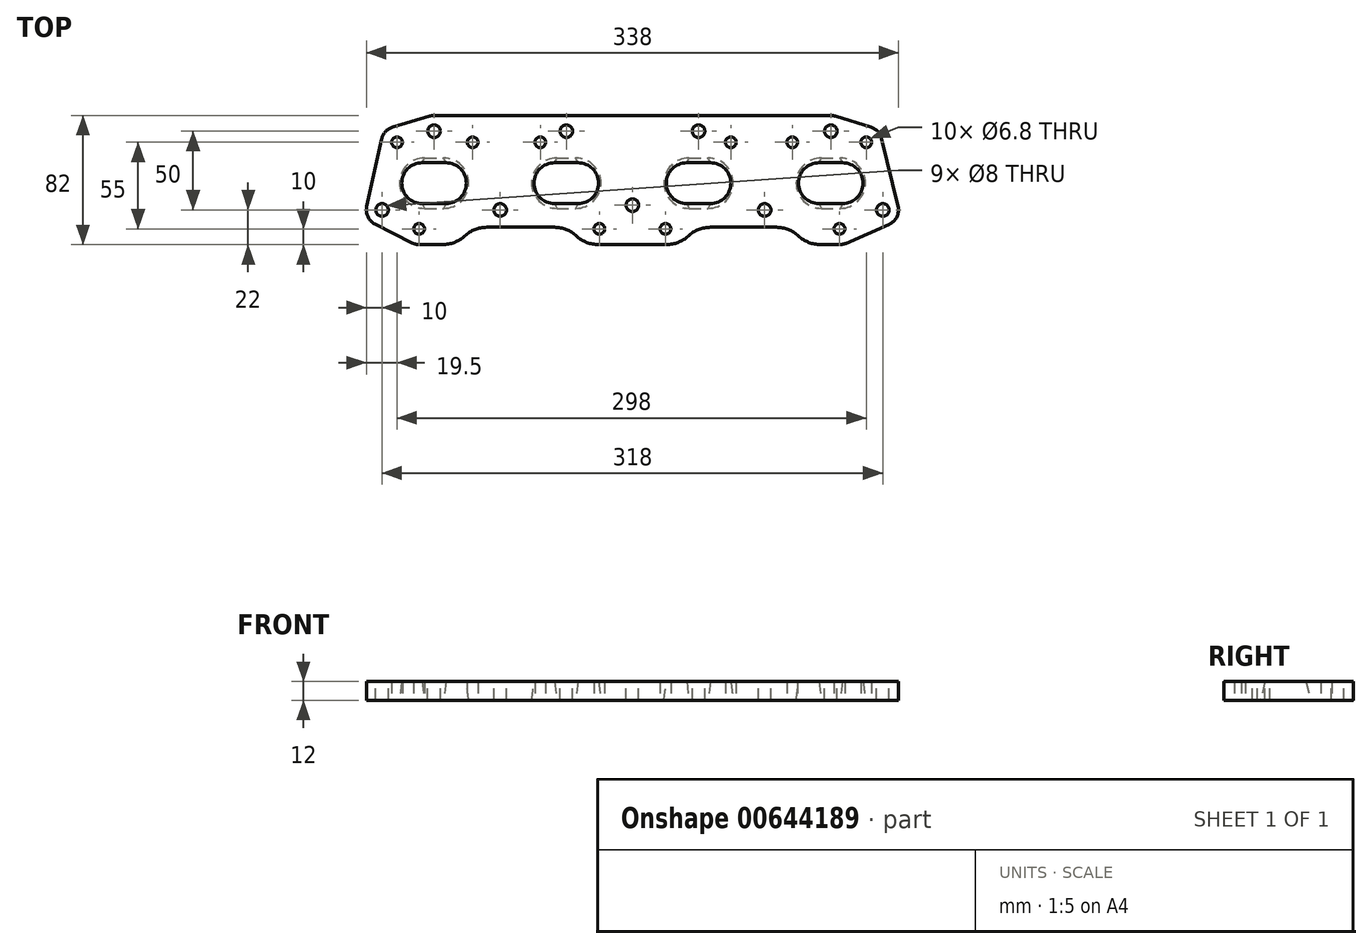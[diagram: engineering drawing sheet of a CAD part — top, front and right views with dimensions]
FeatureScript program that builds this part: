
annotation { "Feature Type Name" : "Feature", "Feature Type Description" : "" }
export const myFeature = defineFeature(function(context is Context, id is Id, definition is map)
    precondition{}
    {
        {
            var Q0;
            Q0=qCreatedBy(makeId("Top.planeOp"),FACE);
            var sketch = newSketch(context, id + "F0", { "sketchPlane" : qUnion([Q0])});
            skCircle(sketch, "E0", {"center": v(-17.5, 26) * mm, "radius": 5 * mm, "construction": true});
            skCircle(sketch, "E1", {"center": v(-3.5, -29) * mm, "radius": 5 * mm, "construction": true});
            skCircle(sketch, "E2", {"center": v(30.5, 26) * mm, "radius": 5 * mm, "construction": true});
            skCircle(sketch, "E3", {"center": v(73.5, 26) * mm, "radius": 5 * mm, "construction": true});
            skCircle(sketch, "E4", {"center": v(194.5, 26) * mm, "radius": 5 * mm, "construction": true});
            skCircle(sketch, "E5", {"center": v(233.5, 26) * mm, "radius": 5 * mm, "construction": true});
            skCircle(sketch, "E6", {"center": v(280.5, 26) * mm, "radius": 4 * mm, "construction": true});
            skCircle(sketch, "E7", {"center": v(111, -29) * mm, "radius": 4 * mm, "construction": true});
            skCircle(sketch, "E8", {"center": v(153, -29) * mm, "radius": 5 * mm, "construction": true});
            skCircle(sketch, "E9", {"center": v(263.5, -29) * mm, "radius": 5 * mm, "construction": true});
            skLineSegment(sketch, "E10", {"start": v(0, 0) * mm, "end": v(46.38, 0) * mm, "construction": true});
            skCircle(sketch, "E11", {"center": v(-17.5, 26) * mm, "radius": 10 * mm, "construction": true});
            skCircle(sketch, "E12", {"center": v(-3.5, -29) * mm, "radius": 10 * mm, "construction": true});
            skCircle(sketch, "E13", {"center": v(263.5, -29) * mm, "radius": 10 * mm, "construction": true});
            skCircle(sketch, "E14", {"center": v(280.5, 26) * mm, "radius": 10 * mm, "construction": true});
            skCircle(sketch, "E15", {"center": v(6, 33) * mm, "radius": 4 * mm, "construction": true});
            skCircle(sketch, "E16", {"center": v(-27, -17) * mm, "radius": 4 * mm, "construction": true});
            skCircle(sketch, "E17", {"center": v(90, 33) * mm, "radius": 4 * mm, "construction": true});
            skCircle(sketch, "E18", {"center": v(174, 33) * mm, "radius": 4 * mm, "construction": true});
            skCircle(sketch, "E19", {"center": v(258, 33) * mm, "radius": 4 * mm, "construction": true});
            skCircle(sketch, "E20", {"center": v(48, -17) * mm, "radius": 4 * mm, "construction": true});
            skCircle(sketch, "E21", {"center": v(132, -14) * mm, "radius": 4 * mm, "construction": true});
            skCircle(sketch, "E22", {"center": v(216, -17) * mm, "radius": 4 * mm, "construction": true});
            skCircle(sketch, "E23", {"center": v(291, -17) * mm, "radius": 4 * mm, "construction": true});
            skCircle(sketch, "E24", {"center": v(6, 33) * mm, "radius": 10 * mm, "construction": true});
            skCircle(sketch, "E25", {"center": v(258, 33) * mm, "radius": 10 * mm, "construction": true});
            skCircle(sketch, "E26", {"center": v(-27, -17) * mm, "radius": 10 * mm, "construction": true});
            skCircle(sketch, "E27", {"center": v(291, -17) * mm, "radius": 10 * mm, "construction": true});
            skLineSegment(sketch, "E28", {"start": v(3.15, 42.58) * mm, "end": v(-20.35, 35.58) * mm});
            skLineSegment(sketch, "E29", {"start": v(-27.26, 28.16) * mm, "end": v(-36.76, -14.84) * mm});
            skLineSegment(sketch, "E30", {"start": v(-31.55, -25.9) * mm, "end": v(-8.05, -37.9) * mm});
            skLineSegment(sketch, "E31", {"start": v(267.5, -38.17) * mm, "end": v(295, -26.17) * mm});
            skLineSegment(sketch, "E32", {"start": v(300.71, -14.63) * mm, "end": v(290.21, 28.37) * mm});
            skLineSegment(sketch, "E33", {"start": v(283.47, 35.55) * mm, "end": v(260.97, 42.55) * mm});
            skArc(sketch, "E34", {"start": v(6, 43) * mm, "mid": v(4.56, 42.9) * mm, "end": v(3.15, 42.58) * mm});
            skArc(sketch, "E35", {"start": v(-20.35, 35.58) * mm, "mid": v(-24.82, 32.81) * mm, "end": v(-27.26, 28.16) * mm});
            skArc(sketch, "E36", {"start": v(-36.76, -14.84) * mm, "mid": v(-36.04, -21.26) * mm, "end": v(-31.55, -25.9) * mm});
            skArc(sketch, "E37", {"start": v(-8.05, -37.9) * mm, "mid": v(-5.84, -38.72) * mm, "end": v(-3.5, -39) * mm});
            skArc(sketch, "E38", {"start": v(263.45, -39) * mm, "mid": v(265.52, -38.8) * mm, "end": v(267.5, -38.17) * mm});
            skArc(sketch, "E39", {"start": v(295, -26.17) * mm, "mid": v(299.96, -21.44) * mm, "end": v(300.71, -14.63) * mm});
            skArc(sketch, "E40", {"start": v(290.21, 28.37) * mm, "mid": v(287.79, 32.85) * mm, "end": v(283.47, 35.55) * mm});
            skArc(sketch, "E41", {"start": v(260.97, 42.55) * mm, "mid": v(259.5, 42.89) * mm, "end": v(258, 43) * mm});
            skLineSegment(sketch, "E42", {"start": v(-67.09, -28) * mm, "end": v(306.12, -28) * mm, "construction": true});
            skLineSegment(sketch, "E43", {"start": v(-3.5, -39) * mm, "end": v(11.5, -39) * mm});
            skLineSegment(sketch, "E44", {"start": v(263.45, -39) * mm, "end": v(251.45, -39) * mm});
            skLineSegment(sketch, "E45", {"start": v(110.44, -39) * mm, "end": v(153.53, -39) * mm});
            skLineSegment(sketch, "E46", {"start": v(-51.35, -33.5) * mm, "end": v(297.43, -33.5) * mm, "construction": true});
            skArc(sketch, "E47", {"start": v(11.5, -39) * mm, "mid": v(19.02, -37.58) * mm, "end": v(25.5, -33.5) * mm});
            skArc(sketch, "E48", {"start": v(39.5, -28) * mm, "mid": v(31.98, -29.42) * mm, "end": v(25.5, -33.5) * mm});
            skArc(sketch, "E49", {"start": v(96.44, -33.5) * mm, "mid": v(102.92, -37.58) * mm, "end": v(110.44, -39) * mm});
            skArc(sketch, "E50", {"start": v(96.44, -33.5) * mm, "mid": v(89.96, -29.42) * mm, "end": v(82.44, -28) * mm});
            skArc(sketch, "E51", {"start": v(153.53, -39) * mm, "mid": v(161.05, -37.58) * mm, "end": v(167.53, -33.5) * mm});
            skArc(sketch, "E52", {"start": v(181.53, -28) * mm, "mid": v(174, -29.42) * mm, "end": v(167.53, -33.5) * mm});
            skArc(sketch, "E53", {"start": v(237.45, -33.5) * mm, "mid": v(243.92, -37.58) * mm, "end": v(251.45, -39) * mm});
            skArc(sketch, "E54", {"start": v(237.45, -33.5) * mm, "mid": v(230.97, -29.42) * mm, "end": v(223.45, -28) * mm});
            skLineSegment(sketch, "E55", {"start": v(39.5, -28) * mm, "end": v(82.44, -28) * mm});
            skLineSegment(sketch, "E56", {"start": v(181.53, -28) * mm, "end": v(223.45, -28) * mm});
            skLineSegment(sketch, "E57", {"start": v(258, 43) * mm, "end": v(6, 43) * mm});
            skSolve(sketch);
        }
        {
            var Q0;
            Q0=qCreatedBy(makeId("Top.planeOp"),FACE);
            var sketch = newSketch(context, id + "F1", { "sketchPlane" : qUnion([Q0])});
            skArc(sketch, "E58", {"start": v(0, 16) * mm, "mid": v(-16, 0) * mm, "end": v(0, -16) * mm});
            skLineSegment(sketch, "E59", {"start": v(0, 16) * mm, "end": v(12, 16) * mm});
            skArc(sketch, "E60", {"start": v(12, -16) * mm, "mid": v(28, 0) * mm, "end": v(12, 16) * mm});
            skLineSegment(sketch, "E61", {"start": v(0, -16) * mm, "end": v(12, -16) * mm});
            skArc(sketch, "E62.1.0.0", {"start": v(96, -16) * mm, "mid": v(112, 0) * mm, "end": v(96, 16) * mm});
            skArc(sketch, "E62.1.0.1", {"start": v(84, 16) * mm, "mid": v(68, 0) * mm, "end": v(84, -16) * mm});
            skLineSegment(sketch, "E62.1.0.2", {"start": v(84, -16) * mm, "end": v(96, -16) * mm});
            skLineSegment(sketch, "E62.1.0.3", {"start": v(84, 16) * mm, "end": v(96, 16) * mm});
            skArc(sketch, "E62.2.0.0", {"start": v(180, -16) * mm, "mid": v(196, 0) * mm, "end": v(180, 16) * mm});
            skArc(sketch, "E62.2.0.1", {"start": v(168, 16) * mm, "mid": v(152, 0) * mm, "end": v(168, -16) * mm});
            skLineSegment(sketch, "E62.2.0.2", {"start": v(168, -16) * mm, "end": v(180, -16) * mm});
            skLineSegment(sketch, "E62.2.0.3", {"start": v(168, 16) * mm, "end": v(180, 16) * mm});
            skArc(sketch, "E62.3.0.0", {"start": v(264, -16) * mm, "mid": v(280, 0) * mm, "end": v(264, 16) * mm});
            skArc(sketch, "E62.3.0.1", {"start": v(252, 16) * mm, "mid": v(236, 0) * mm, "end": v(252, -16) * mm});
            skLineSegment(sketch, "E62.3.0.2", {"start": v(252, -16) * mm, "end": v(264, -16) * mm});
            skLineSegment(sketch, "E62.3.0.3", {"start": v(252, 16) * mm, "end": v(264, 16) * mm});
            skLineSegment(sketch, "E62.direction1", {"start": v(0, -16) * mm, "end": v(84, -16) * mm, "construction": true});
            skCircle(sketch, "E63", {"center": v(6, 33) * mm, "radius": 4 * mm});
            skCircle(sketch, "E64", {"center": v(-27, -17) * mm, "radius": 4 * mm});
            skCircle(sketch, "E65", {"center": v(90, 33) * mm, "radius": 4 * mm});
            skCircle(sketch, "E66", {"center": v(174, 33) * mm, "radius": 4 * mm});
            skCircle(sketch, "E67", {"center": v(258, 33) * mm, "radius": 4 * mm});
            skCircle(sketch, "E68", {"center": v(48, -17) * mm, "radius": 4 * mm});
            skCircle(sketch, "E69", {"center": v(132, -14) * mm, "radius": 4 * mm});
            skCircle(sketch, "E70", {"center": v(216, -17) * mm, "radius": 4 * mm});
            skCircle(sketch, "E71", {"center": v(291, -17) * mm, "radius": 4 * mm});
            skSolve(sketch);
        }
        {
            var Q0;
            Q0=qCreatedBy(makeId("Top.planeOp"),FACE);
            cPlane(context, id + "F2", {"entities" : qUnion([Q0]), "cplaneType" : CPlaneType.OFFSET, "offset" : 12 * mm, "width" : 150 * mm, "height" : 150 * mm});
        }
        {
            var Q0;
            Q0=qCreatedBy(id+"F2.planeOp",FACE);
            var sketch = newSketch(context, id + "F3", { "sketchPlane" : qUnion([Q0]), "disableImprinting" : false});
            skCircle(sketch, "E72", {"center": v(-17.5, 26) * mm, "radius": 5 * mm});
            skCircle(sketch, "E73", {"center": v(-3.5, -29) * mm, "radius": 5 * mm});
            skCircle(sketch, "E74", {"center": v(30.5, 26) * mm, "radius": 5 * mm});
            skCircle(sketch, "E75", {"center": v(73.5, 26) * mm, "radius": 5 * mm});
            skCircle(sketch, "E76", {"center": v(194.5, 26) * mm, "radius": 5 * mm});
            skCircle(sketch, "E77", {"center": v(233.5, 26) * mm, "radius": 5 * mm});
            skCircle(sketch, "E78", {"center": v(280.5, 26) * mm, "radius": 4 * mm});
            skCircle(sketch, "E79", {"center": v(111, -29) * mm, "radius": 4 * mm});
            skCircle(sketch, "E80", {"center": v(153, -29) * mm, "radius": 5 * mm});
            skCircle(sketch, "E81", {"center": v(263.5, -29) * mm, "radius": 5 * mm});
            skArc(sketch, "E82", {"start": v(-1.5, 13) * mm, "mid": v(-14.5, 0) * mm, "end": v(-1.5, -13) * mm});
            skArc(sketch, "E83", {"start": v(13.5, -13) * mm, "mid": v(26.5, 0) * mm, "end": v(13.5, 13) * mm});
            skArc(sketch, "E84", {"start": v(97.5, -13) * mm, "mid": v(110.5, 0) * mm, "end": v(97.5, 13) * mm});
            skArc(sketch, "E85", {"start": v(82.5, 13) * mm, "mid": v(69.5, 0) * mm, "end": v(82.5, -13) * mm});
            skArc(sketch, "E86", {"start": v(181.5, -13) * mm, "mid": v(194.5, 0) * mm, "end": v(181.5, 13) * mm});
            skArc(sketch, "E87", {"start": v(166.5, 13) * mm, "mid": v(153.5, 0) * mm, "end": v(166.5, -13) * mm});
            skArc(sketch, "E88", {"start": v(265.5, -13) * mm, "mid": v(278.5, 0) * mm, "end": v(265.5, 13) * mm});
            skArc(sketch, "E89", {"start": v(250.5, 13) * mm, "mid": v(237.5, 0) * mm, "end": v(250.5, -13) * mm});
            skLineSegment(sketch, "E90", {"start": v(-1.5, 13) * mm, "end": v(13.5, 13) * mm});
            skLineSegment(sketch, "E91", {"start": v(-1.5, -13) * mm, "end": v(13.5, -13) * mm});
            skLineSegment(sketch, "E92", {"start": v(82.5, 13) * mm, "end": v(97.5, 13) * mm});
            skLineSegment(sketch, "E93", {"start": v(82.5, -13) * mm, "end": v(97.5, -13) * mm});
            skLineSegment(sketch, "E94", {"start": v(166.5, 13) * mm, "end": v(181.5, 13) * mm});
            skLineSegment(sketch, "E95", {"start": v(166.5, -13) * mm, "end": v(181.5, -13) * mm});
            skLineSegment(sketch, "E96", {"start": v(250.5, 13) * mm, "end": v(265.5, 13) * mm});
            skLineSegment(sketch, "E97", {"start": v(250.5, -13) * mm, "end": v(265.5, -13) * mm});
            skLineSegment(sketch, "E98", {"start": v(-34.95, 26) * mm, "end": v(-28, 26) * mm, "construction": true});
            skLineSegment(sketch, "E99", {"start": v(-38.64, -29) * mm, "end": v(-22.87, -29) * mm, "construction": true});
            skLineSegment(sketch, "E100", {"start": v(-41.55, 0) * mm, "end": v(-21.62, 0) * mm, "construction": true});
            skSolve(sketch);
        }
        {
            var Q0;
            Q0 = qSketchRegion(id + "F0", true);
            extrude(context, id + "F4", {"entities" : qUnion([Q0]), "depth" : 12 * mm, "offsetDistance" : 25 * mm});
        }
        {
            var Q1;
            Q1=makeQuery(id+"F3.imprint","IMPRINT",FACE,{"disambiguationData":[TD([[makeQuery(id+"F3.imprint","IMPRINT",EDGE,{"derivedFrom":sQuery(id+"F3.wireOp",EDGE,"E82")}),1.0]])]});
            var Q2;
            Q2=makeQuery(id+"F1.imprint","IMPRINT",FACE,{"disambiguationData":[TD([[makeQuery(id+"F1.imprint","IMPRINT",EDGE,{"derivedFrom":sQuery(id+"F1.wireOp",EDGE,"E58")}),1.0]])]});
            loft(context, id + "F5", {"operationType" : NewBodyOperationType.REMOVE, "sheetProfilesArray" : [{ "sheetProfileEntities" : qUnion([Q1]) }, { "sheetProfileEntities" : qUnion([Q2]) }]});
        }
        {
            var Q1;
            Q1=makeQuery(id+"F3.imprint","IMPRINT",FACE,{"disambiguationData":[TD([[makeQuery(id+"F3.imprint","IMPRINT",EDGE,{"derivedFrom":sQuery(id+"F3.wireOp",EDGE,"E84")}),1.0]])]});
            var Q2;
            Q2=makeQuery(id+"F1.imprint","IMPRINT",FACE,{"disambiguationData":[TD([[makeQuery(id+"F1.imprint","IMPRINT",EDGE,{"derivedFrom":sQuery(id+"F1.wireOp",EDGE,"E62.1.0.0")}),1.0]])]});
            loft(context, id + "F6", {"operationType" : NewBodyOperationType.REMOVE, "sheetProfilesArray" : [{ "sheetProfileEntities" : qUnion([Q1]) }, { "sheetProfileEntities" : qUnion([Q2]) }]});
        }
        {
            var Q1;
            Q1=makeQuery(id+"F3.imprint","IMPRINT",FACE,{"disambiguationData":[TD([[makeQuery(id+"F3.imprint","IMPRINT",EDGE,{"derivedFrom":sQuery(id+"F3.wireOp",EDGE,"E86")}),1.0]])]});
            var Q2;
            Q2=makeQuery(id+"F1.imprint","IMPRINT",FACE,{"disambiguationData":[TD([[makeQuery(id+"F1.imprint","IMPRINT",EDGE,{"derivedFrom":sQuery(id+"F1.wireOp",EDGE,"E62.2.0.0")}),1.0]])]});
            loft(context, id + "F7", {"operationType" : NewBodyOperationType.REMOVE, "sheetProfilesArray" : [{ "sheetProfileEntities" : qUnion([Q1]) }, { "sheetProfileEntities" : qUnion([Q2]) }]});
        }
        {
            var Q1;
            Q1=makeQuery(id+"F3.imprint","IMPRINT",FACE,{"disambiguationData":[TD([[makeQuery(id+"F3.imprint","IMPRINT",EDGE,{"derivedFrom":sQuery(id+"F3.wireOp",EDGE,"E88")}),1.0]])]});
            var Q2;
            Q2=makeQuery(id+"F1.imprint","IMPRINT",FACE,{"disambiguationData":[TD([[makeQuery(id+"F1.imprint","IMPRINT",EDGE,{"derivedFrom":sQuery(id+"F1.wireOp",EDGE,"E62.3.0.0")}),1.0]])]});
            loft(context, id + "F8", {"operationType" : NewBodyOperationType.REMOVE, "sheetProfilesArray" : [{ "sheetProfileEntities" : qUnion([Q1]) }, { "sheetProfileEntities" : qUnion([Q2]) }]});
        }
        {
            var Q0;
            Q0=sQuery(id+"F1.wireOp",VERTEX,"E64.center");
            var Q1;
            Q1=sQuery(id+"F1.wireOp",VERTEX,"E68.center");
            var Q2;
            Q2=sQuery(id+"F1.wireOp",VERTEX,"E63.center");
            var Q3;
            Q3=sQuery(id+"F1.wireOp",VERTEX,"E65.center");
            var Q4;
            Q4=sQuery(id+"F1.wireOp",VERTEX,"E69.center");
            var Q5;
            Q5=sQuery(id+"F1.wireOp",VERTEX,"E66.center");
            var Q6;
            Q6=sQuery(id+"F1.wireOp",VERTEX,"E70.center");
            var Q7;
            Q7=sQuery(id+"F1.wireOp",VERTEX,"E71.center");
            var Q8;
            Q8=sQuery(id+"F1.wireOp",VERTEX,"E67.center");
            var Q9;
            Q9=makeQuery(id+"F4.opExtrude","SWEPT_BODY",BODY,{"disambiguationData":[OSD([sQuery(id+"F0.wireOp",EDGE,"pKSUJSgC-n6HE-i7VQ-AnP0-U6Q0sxJJ8JBK"),sQuery(id+"F0.wireOp",EDGE,"HsRLkKV4-NUN3-DtmZ-hMzP-qN3fu05NwNyH"),sQuery(id+"F0.wireOp",EDGE,"E28"),sQuery(id+"F0.wireOp",EDGE,"E29"),sQuery(id+"F0.wireOp",EDGE,"E30"),sQuery(id+"F0.wireOp",EDGE,"E31"),sQuery(id+"F0.wireOp",EDGE,"E32"),sQuery(id+"F0.wireOp",EDGE,"E33"),sQuery(id+"F0.wireOp",EDGE,"E34"),sQuery(id+"F0.wireOp",EDGE,"E35"),sQuery(id+"F0.wireOp",EDGE,"E36"),sQuery(id+"F0.wireOp",EDGE,"E37"),sQuery(id+"F0.wireOp",EDGE,"E38"),sQuery(id+"F0.wireOp",EDGE,"E39"),sQuery(id+"F0.wireOp",EDGE,"E40"),sQuery(id+"F0.wireOp",EDGE,"E41")])]});
            hole(context, id + "F9", {"style" : HoleStyle.SIMPLE, "endStyle" : HoleEndStyle.THROUGH, "oppositeDirection" : true, "holeDiameter" : 8 * mm, "majorDiameter" : 5 * mm, "isTappedThrough" : true, "tappedDepth" : 12 * mm, "tapClearance" : 3, "locations" : qUnion([Q0, Q1, Q2, Q3, Q4, Q5, Q6, Q7, Q8]), "scope" : qUnion([Q9]), "startStyle" : HoleStartStyle.PART});
        }
        {
            var Q0;
            Q0=sQuery(id+"F3.wireOp",VERTEX,"E73.center");
            var Q1;
            Q1=sQuery(id+"F3.wireOp",VERTEX,"E72.center");
            var Q2;
            Q2=sQuery(id+"F3.wireOp",VERTEX,"E74.center");
            var Q3;
            Q3=sQuery(id+"F3.wireOp",VERTEX,"E75.center");
            var Q4;
            Q4=sQuery(id+"F3.wireOp",VERTEX,"E76.center");
            var Q5;
            Q5=sQuery(id+"F3.wireOp",VERTEX,"E77.center");
            var Q6;
            Q6=sQuery(id+"F3.wireOp",VERTEX,"E81.center");
            var Q7;
            Q7=sQuery(id+"F3.wireOp",VERTEX,"E80.center");
            var Q8;
            Q8=makeQuery(id+"F4.opExtrude","SWEPT_BODY",BODY,{"disambiguationData":[OSD([sQuery(id+"F0.wireOp",EDGE,"pKSUJSgC-n6HE-i7VQ-AnP0-U6Q0sxJJ8JBK"),sQuery(id+"F0.wireOp",EDGE,"HsRLkKV4-NUN3-DtmZ-hMzP-qN3fu05NwNyH"),sQuery(id+"F0.wireOp",EDGE,"E28"),sQuery(id+"F0.wireOp",EDGE,"E29"),sQuery(id+"F0.wireOp",EDGE,"E30"),sQuery(id+"F0.wireOp",EDGE,"E31"),sQuery(id+"F0.wireOp",EDGE,"E32"),sQuery(id+"F0.wireOp",EDGE,"E33"),sQuery(id+"F0.wireOp",EDGE,"E34"),sQuery(id+"F0.wireOp",EDGE,"E35"),sQuery(id+"F0.wireOp",EDGE,"E36"),sQuery(id+"F0.wireOp",EDGE,"E37"),sQuery(id+"F0.wireOp",EDGE,"E38"),sQuery(id+"F0.wireOp",EDGE,"E39"),sQuery(id+"F0.wireOp",EDGE,"E40"),sQuery(id+"F0.wireOp",EDGE,"E41")])]});
            hole(context, id + "F10", {"style" : HoleStyle.SIMPLE, "endStyle" : HoleEndStyle.THROUGH, "standardTappedOrClearance" : lookupTablePath({ "standard" : "ISO", "engagement" : "75%", "pitch" : "1.25 mm", "size" : "M8", "type" : "Tapped" }), "standardBlindInLast" : lookupTablePath({ "standard" : "ISO", "fit" : "Normal", "engagement" : "75%", "pitch" : "1.25 mm", "size" : "M8", "type" : "Clearance & tapped" }), "holeDiameter" : 6.8 * mm, "majorDiameter" : 8 * mm, "showTappedDepth" : true, "isTappedThrough" : true, "tappedDepth" : 12 * mm, "tapClearance" : 3, "locations" : qUnion([Q0, Q1, Q2, Q3, Q4, Q5, Q6, Q7]), "scope" : qUnion([Q8]), "startStyle" : HoleStartStyle.PART});
        }
        {
            var Q0;
            Q0=sQuery(id+"F3.wireOp",VERTEX,"E79.center");
            var Q1;
            Q1=sQuery(id+"F3.wireOp",VERTEX,"E78.center");
            var Q2;
            Q2=makeQuery(id+"F4.opExtrude","SWEPT_BODY",BODY,{"disambiguationData":[OSD([sQuery(id+"F0.wireOp",EDGE,"pKSUJSgC-n6HE-i7VQ-AnP0-U6Q0sxJJ8JBK"),sQuery(id+"F0.wireOp",EDGE,"HsRLkKV4-NUN3-DtmZ-hMzP-qN3fu05NwNyH"),sQuery(id+"F0.wireOp",EDGE,"E28"),sQuery(id+"F0.wireOp",EDGE,"E29"),sQuery(id+"F0.wireOp",EDGE,"E30"),sQuery(id+"F0.wireOp",EDGE,"E31"),sQuery(id+"F0.wireOp",EDGE,"E32"),sQuery(id+"F0.wireOp",EDGE,"E33"),sQuery(id+"F0.wireOp",EDGE,"E34"),sQuery(id+"F0.wireOp",EDGE,"E35"),sQuery(id+"F0.wireOp",EDGE,"E36"),sQuery(id+"F0.wireOp",EDGE,"E37"),sQuery(id+"F0.wireOp",EDGE,"E38"),sQuery(id+"F0.wireOp",EDGE,"E39"),sQuery(id+"F0.wireOp",EDGE,"E40"),sQuery(id+"F0.wireOp",EDGE,"E41")])]});
            hole(context, id + "F11", {"style" : HoleStyle.SIMPLE, "endStyle" : HoleEndStyle.THROUGH, "standardTappedOrClearance" : lookupTablePath({ "standard" : "ISO", "engagement" : "75%", "pitch" : "1.25 mm", "size" : "M8", "type" : "Tapped" }), "standardBlindInLast" : lookupTablePath({ "standard" : "ISO", "engagement" : "75%", "pitch" : "1.25 mm", "size" : "M8", "type" : "Tapped" }), "holeDiameter" : 6.8 * mm, "majorDiameter" : 8 * mm, "showTappedDepth" : true, "isTappedThrough" : true, "tappedDepth" : 12 * mm, "tapClearance" : 3, "locations" : qUnion([Q0, Q1]), "scope" : qUnion([Q2]), "startStyle" : HoleStartStyle.PART});
        }
    });
